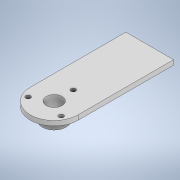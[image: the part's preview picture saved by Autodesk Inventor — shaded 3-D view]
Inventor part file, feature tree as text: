
AUTODESK INVENTOR PART (.ipt)
format: ipt  version: 2020.2 (Build 242310000, 310)  size: 130,560 bytes
history: native  units: in
note: dims shown in document units (in); Inventor stores cm internally (conversion verified against a paired STEP export)
features: extrude x2, sketch x2
ambient origin geometry x8: Origin, YZ Plane, XZ Plane, XY Plane, X Axis, Y Axis, Z Axis, Center Point
bodies: Body1 (feature_tree)
feature tree (4):
  extrude  "Extrusion2"  Depth=0.15in TaperAngle=360.0deg
  extrude  "Extrusion3"  Depth=0.15in TaperAngle=0.0deg
  sketch  "Sketch1"  dims[d1=0.15in d2=1.1811in d4=360.0deg]
  sketch  "Sketch2"  dims[d12=0.5in d13=0.15in d14=0.0in d15=0.75in d16=0.375in d17=0.0in]
